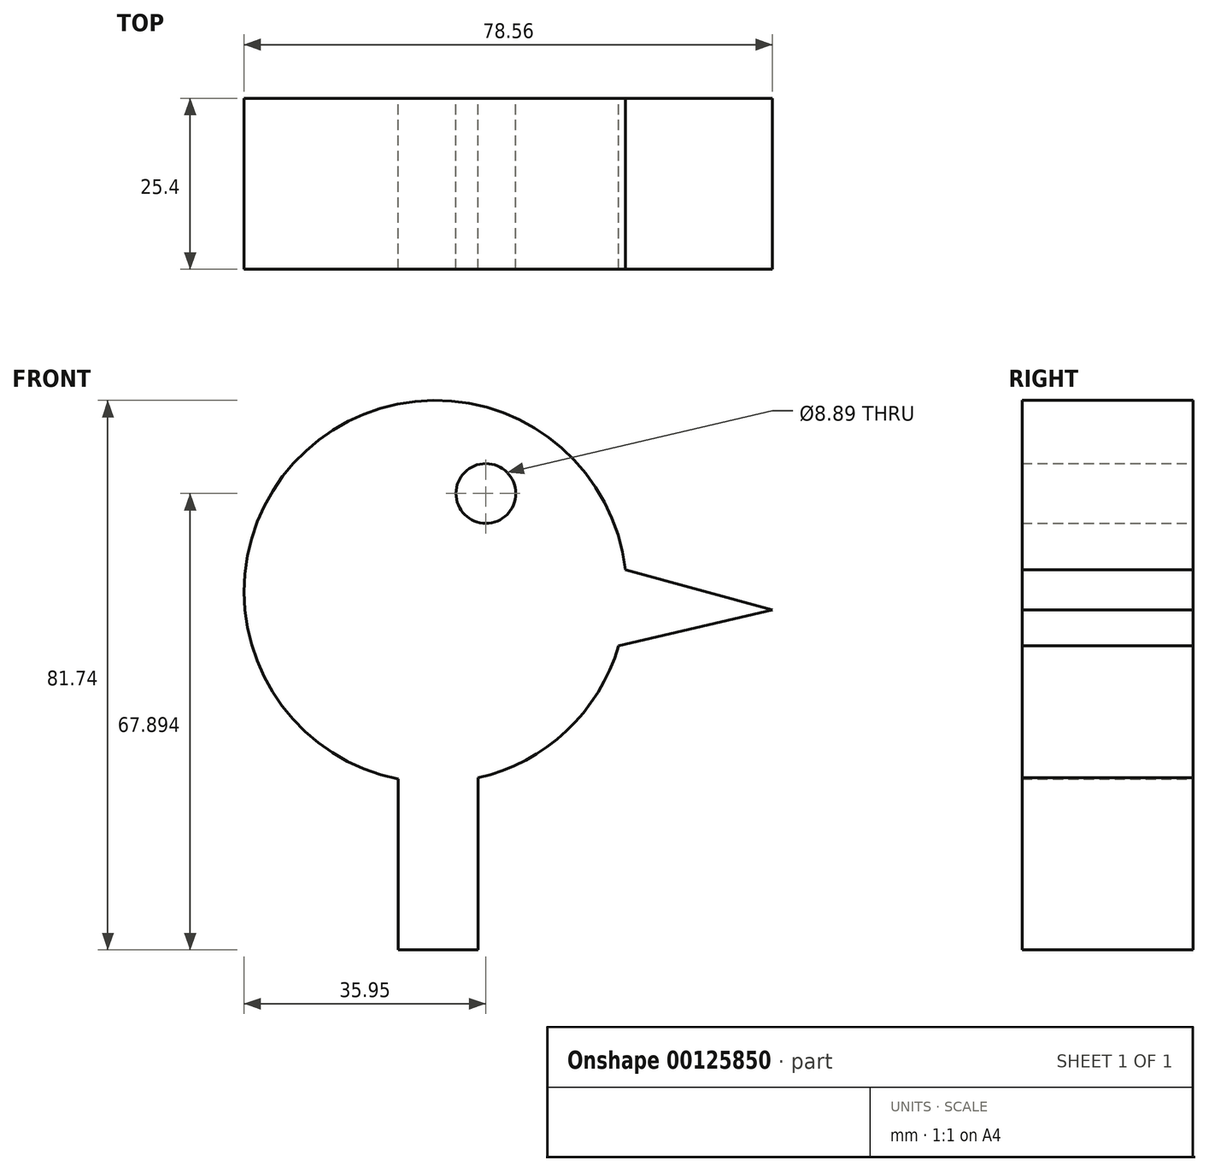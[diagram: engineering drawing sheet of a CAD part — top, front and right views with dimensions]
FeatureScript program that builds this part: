
annotation { "Feature Type Name" : "Feature", "Feature Type Description" : "" }
export const myFeature = defineFeature(function(context is Context, id is Id, definition is map)
    precondition{}
    {
        {
            var Q0;
            Q0=qCreatedBy(makeId("Front.planeOp"),FACE);
            var sketch = newSketch(context, id + "F0", { "sketchPlane" : qUnion([Q0])});
            skCircle(sketch, "E0", {"center": v(0, 0) * mm, "radius": 28.44 * mm});
            skCircle(sketch, "E1", {"center": v(7.51, 14.6) * mm, "radius": 4.45 * mm});
            skLineSegment(sketch, "E2", {"start": v(28.25, 3.23) * mm, "end": v(50.12, -2.74) * mm});
            skLineSegment(sketch, "E3", {"start": v(50.12, -2.74) * mm, "end": v(27.26, -8.1) * mm});
            skLineSegment(sketch, "E4", {"start": v(-5.53, -27.9) * mm, "end": v(-5.53, -53.3) * mm});
            skLineSegment(sketch, "E5", {"start": v(-5.53, -53.3) * mm, "end": v(6.37, -53.3) * mm});
            skLineSegment(sketch, "E6", {"start": v(6.37, -53.3) * mm, "end": v(6.37, -27.72) * mm});
            skSolve(sketch);
        }
        {
            var Q0;
            Q0=qSketchRegion(id+"F0",true);
            extrude(context, id + "F1", {"entities" : qUnion([Q0]), "depth" : 25.4 * mm});
        }
    });
